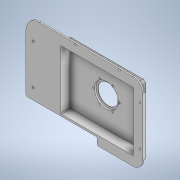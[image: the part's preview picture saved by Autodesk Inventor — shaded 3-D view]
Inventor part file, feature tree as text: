
AUTODESK INVENTOR PART (.ipt)
format: ipt  version: 2022 (Build 260153000, 153)  size: 308,736 bytes
history: native  units: mm
features: extrude x9, sketch x9, projected_geometry x7, other x3, fillet x1, pattern_circular x1, reference x1
ambient origin geometry x8: Origin, YZ Plane, XZ Plane, XY Plane, X Axis, Y Axis, Z Axis, Center Point
bodies: Solid1 (feature_tree)
feature tree (31):
  extrude  "Extrusion1"  Depth=94.5mm
  extrude  "Extrusion2"  Depth=15.0mm TaperAngle=0.0deg
  extrude  "Extrusion3"  Depth=3.0mm
  extrude  "Extrusion4"  Depth=3.0mm
  extrude  "Extrusion7"  Depth=3.0mm
  fillet  "Fillet1"  Radius=66.0mm
  extrude  "Extrusion8"  Depth=7.0mm
  extrude  "Extrusion9"  Depth=17.8mm
  extrude  "Extrusion10"  Depth=2.0mm TaperAngle=0.0deg
  pattern_circular  "Runde Anordnung1"  [2 undecoded]
  extrude  "Extrusion11"  Depth=14.0mm TaperAngle=0.0deg
  sketch  "Sketch1"  dims[d0=115.0mm d1=94.5mm]
  sketch  "Sketch2"  dims[d2=4.0mm d3=15.0mm d4=0.0mm]
  projected_geometry  "Projected Loop1"
  sketch  "Sketch3"  dims[d5=11.0mm d6=3.0mm]
  projected_geometry  "Projected Loop2"
  sketch  "Sketch4"  dims[d7=3.0mm d8=3.0mm]
  projected_geometry  "Projected Loop3"
  sketch  "Sketch7"  dims[d9=3.0mm d10=24.0mm d11=66.0mm]
  projected_geometry  "Projected Loop7"
  sketch  "Sketch8"  dims[d12=9.0mm d13=7.0mm]
  projected_geometry  "Projected Loop8"
  sketch  "Skizze9"  dims[d14=7.0mm d15=17.8mm]
  projected_geometry  "Projizierte Kontur9"
  sketch  "Skizze10"  dims[d16=60.0mm d17=2.0mm d18=0.0mm]
  reference  "Referenz1"
  sketch  "Skizze11"  dims[d19=2.5mm d20=0.0mm d21=3.0mm d22=14.0mm d23=0.0mm d34=2.0mm d35=10.0mm d36=0.0mm d37=3.0mm d38=3.0mm d39=160.0mm d40=0.0mm d41=0.0mm d42=2.0mm d43=10.0mm d44=0.0mm d45=30.0mm d46=13.0mm d47=0.0mm d48=2.8mm d49=14.0mm d50=0.0mm d51=60.0mm d52=360.0deg d54=20.0mm d55=36.1mm d56=2.5mm d57=0.0mm]
  projected_geometry  "Projizierte Kontur10"
  other  "Assembly_XYTable_Aliepexress.iam"
  other  "SMLM_Holder_v1:1"
  other  "01_SMLM_Holder_Base:1"
note: 2 required parameter values undecoded (feature->parameter linkage not recoverable at this tier; creation-order binding heuristic only, values carry confidence <= 0.55)
